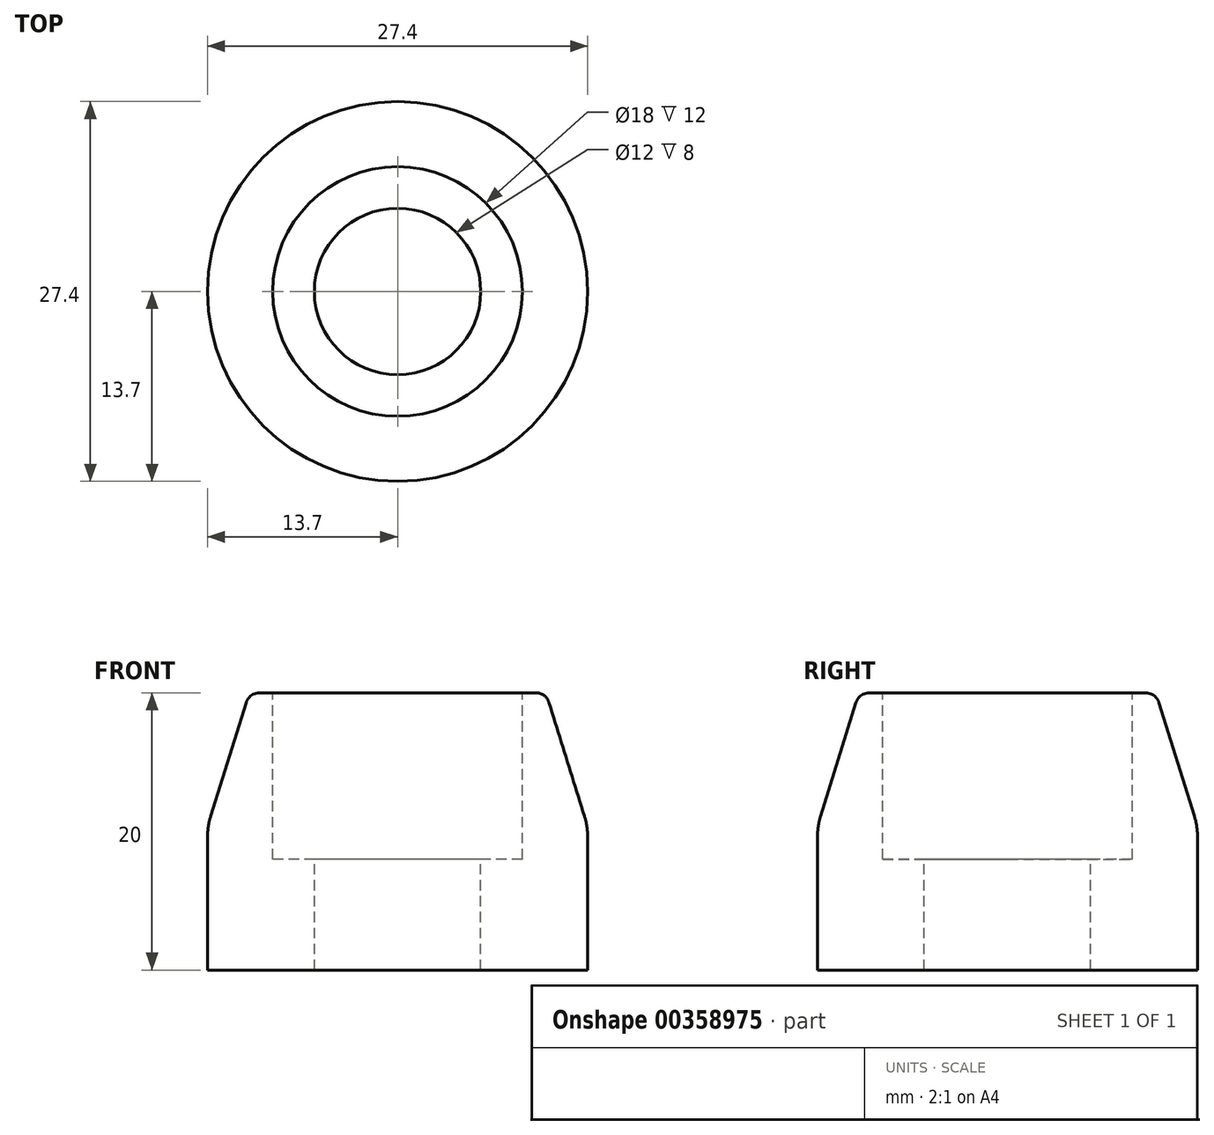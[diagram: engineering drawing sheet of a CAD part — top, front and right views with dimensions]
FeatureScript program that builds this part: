
annotation { "Feature Type Name" : "Feature", "Feature Type Description" : "" }
export const myFeature = defineFeature(function(context is Context, id is Id, definition is map)
    precondition{}
    {
        {
            var Q0;
            Q0=qCreatedBy(makeId("Front.planeOp"),FACE);
            var sketch = newSketch(context, id + "F0", { "sketchPlane" : qUnion([Q0])});
            skLineSegment(sketch, "E0", {"start": v(-6, 0) * mm, "end": v(-13.7, 0) * mm});
            skLineSegment(sketch, "E1", {"start": v(-13.7, 0) * mm, "end": v(-13.7, 9.6) * mm});
            skLineSegment(sketch, "E2", {"start": v(-9.96, 20) * mm, "end": v(-9, 20) * mm});
            skLineSegment(sketch, "E3", {"start": v(-9, 20) * mm, "end": v(-9, 8) * mm});
            skLineSegment(sketch, "E4", {"start": v(-9, 8) * mm, "end": v(-6, 8) * mm});
            skLineSegment(sketch, "E5", {"start": v(0, 24.08) * mm, "end": v(0, -7.58) * mm, "construction": true});
            skPoint(sketch, "E6.visualSharp", {"position": v(-13.7, 20) * mm});
            skLineSegment(sketch, "E7", {"start": v(-6, 8) * mm, "end": v(-6, 0) * mm});
            skLineSegment(sketch, "E8", {"start": v(-10.92, 19.3) * mm, "end": v(-13.47, 11.1) * mm});
            skPoint(sketch, "E9.visualSharp", {"position": v(-13.7, 10.37) * mm});
            skArc(sketch, "E9.filletArc", {"start": v(-13.47, 11.1) * mm, "mid": v(-13.64, 10.36) * mm, "end": v(-13.7, 9.6) * mm});
            skPoint(sketch, "E10.visualSharp", {"position": v(-10.7, 20) * mm});
            skArc(sketch, "E10.filletArc", {"start": v(-9.96, 20) * mm, "mid": v(-10.56, 19.8) * mm, "end": v(-10.92, 19.3) * mm});
            skSolve(sketch);
        }
        {
            var Q0;
            Q0 = qSketchRegion(id + "F0", true);
            var Q1;
            Q1=sQuery(id+"F0.wireOp",EDGE,"E5");
            revolve(context, id + "F1", {"entities" : qUnion([Q0]), "axis" : qUnion([Q1]), "revolveType" : RevolveType.FULL});
        }
    });
